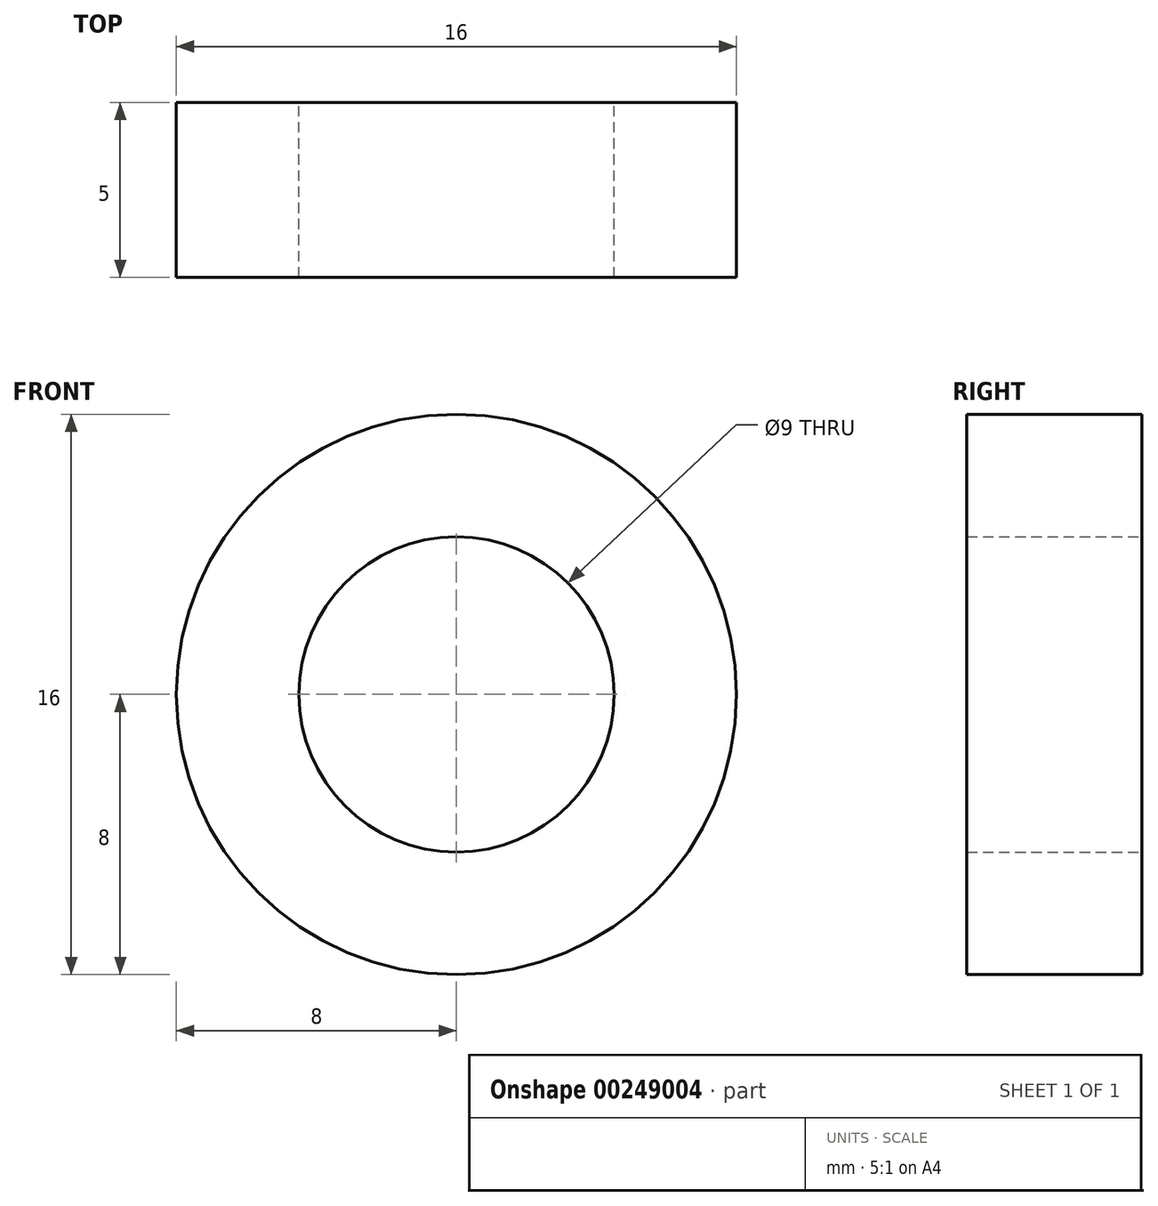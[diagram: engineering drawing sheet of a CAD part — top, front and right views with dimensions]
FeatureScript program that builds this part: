
annotation { "Feature Type Name" : "Feature", "Feature Type Description" : "" }
export const myFeature = defineFeature(function(context is Context, id is Id, definition is map)
    precondition{}
    {
        {
            var Q0;
            Q0=qCreatedBy(makeId("Front.planeOp"),FACE);
            var sketch = newSketch(context, id + "F0", { "sketchPlane" : qUnion([Q0])});
            skCircle(sketch, "E0", {"center": v(0, 0) * mm, "radius": 8 * mm});
            skCircle(sketch, "E1", {"center": v(0, 0) * mm, "radius": 4.5 * mm});
            skSolve(sketch);
        }
        {
            var Q0;
            Q0=makeQuery(id+"F0.imprint","IMPRINT",FACE,{"disambiguationData":[TD([[makeQuery(id+"F0.imprint","IMPRINT",EDGE,{"derivedFrom":sQuery(id+"F0.wireOp",EDGE,"E0")}),1.0]])]});
            extrude(context, id + "F1", {"entities" : qUnion([Q0]), "depth" : 5 * mm});
        }
    });
